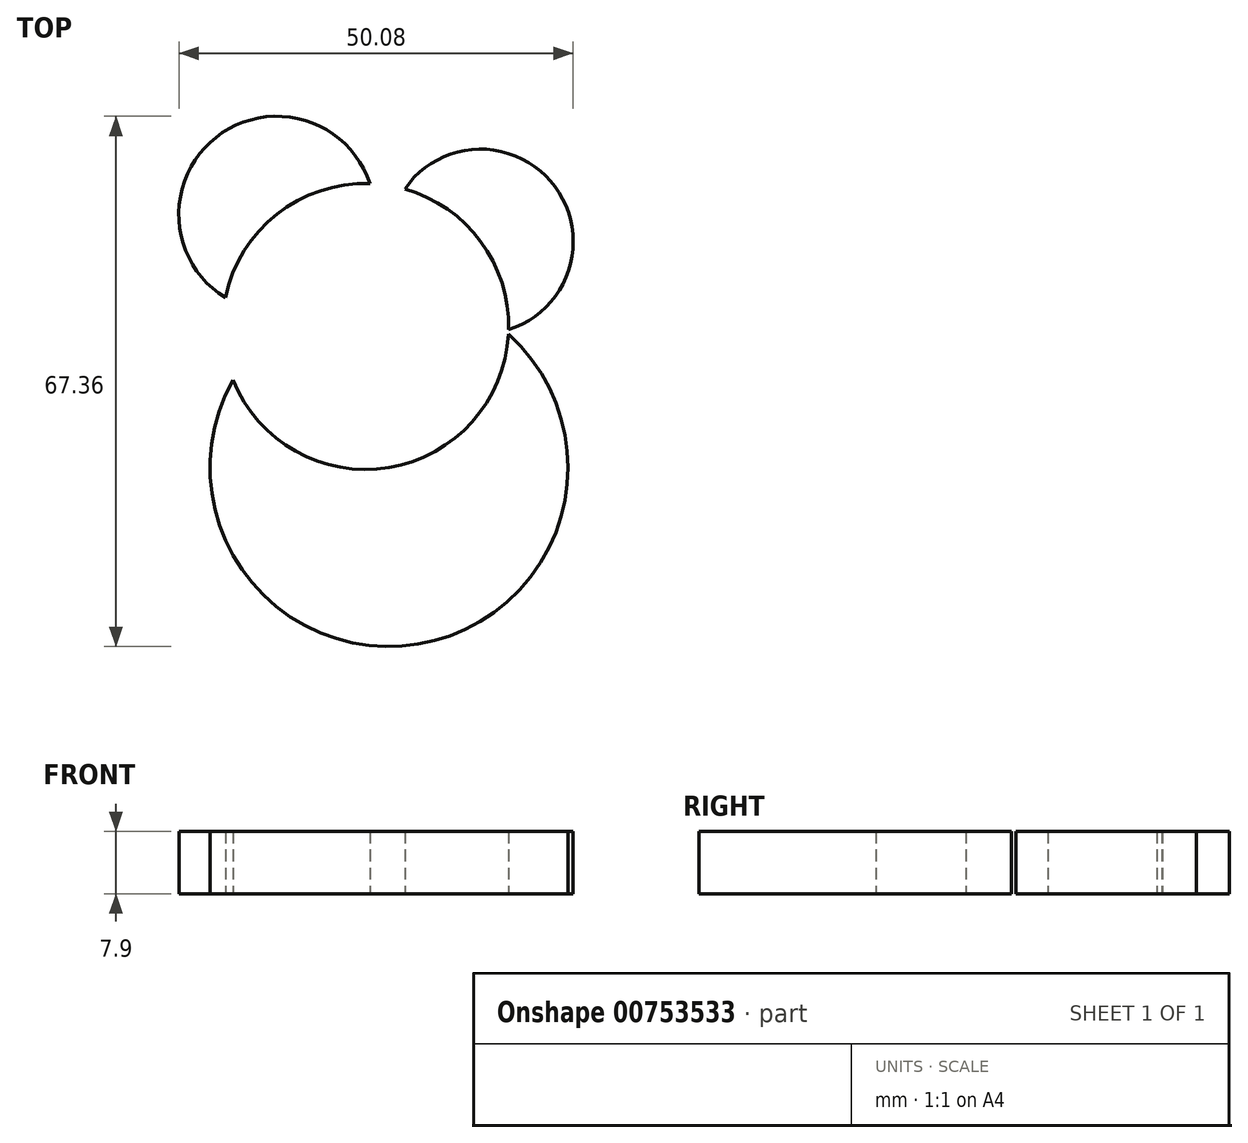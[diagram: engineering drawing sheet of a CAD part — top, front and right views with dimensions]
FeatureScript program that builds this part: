
annotation { "Feature Type Name" : "Feature", "Feature Type Description" : "" }
export const myFeature = defineFeature(function(context is Context, id is Id, definition is map)
    precondition{}
    {
        {
            var Q0;
            Q0=qCreatedBy(makeId("Top.planeOp"),FACE);
            var sketch = newSketch(context, id + "F0", { "sketchPlane" : qUnion([Q0])});
            skCircle(sketch, "E0", {"center": v(0, 0) * mm, "radius": 18.17 * mm});
            skCircle(sketch, "E1", {"center": v(-11.27, 14.25) * mm, "radius": 12.45 * mm});
            skCircle(sketch, "E2", {"center": v(14.62, 10.78) * mm, "radius": 11.74 * mm});
            skCircle(sketch, "E3", {"center": v(2.97, -17.92) * mm, "radius": 22.73 * mm});
            skSolve(sketch);
        }
        {
            var Q0;
            {var subQ0=sQuery(id+"F0.wireOp",EDGE,"E1");var subQ1=sQuery(id+"F0.wireOp",EDGE,"E0");var subQ2=makeQuery(id+"F0.imprint","INTERSECT",VERTEX,{"disambiguationData":[OD(0.0)],"derivedFrom":[subQ1,subQ0]});Q0=makeQuery(id+"F0.imprint","IMPRINT",FACE,{"disambiguationData":[TD([[makeQuery(id+"F0.imprint","IMPRINT",EDGE,{"disambiguationData":[TD([[subQ2,-1.0]])],"derivedFrom":subQ1}),-1.0]])]});}
            var Q1;
            {var subQ0=sQuery(id+"F0.wireOp",EDGE,"E3");var subQ1=sQuery(id+"F0.wireOp",EDGE,"E0");var subQ2=makeQuery(id+"F0.imprint","INTERSECT",VERTEX,{"disambiguationData":[OD(0.0)],"derivedFrom":[subQ1,subQ0]});Q1=makeQuery(id+"F0.imprint","IMPRINT",FACE,{"disambiguationData":[TD([[makeQuery(id+"F0.imprint","IMPRINT",EDGE,{"disambiguationData":[TD([[subQ2,-1.0]])],"derivedFrom":subQ1}),-1.0]])]});}
            var Q2;
            {var subQ0=sQuery(id+"F0.wireOp",EDGE,"E2");var subQ1=sQuery(id+"F0.wireOp",EDGE,"E0");var subQ2=makeQuery(id+"F0.imprint","INTERSECT",VERTEX,{"disambiguationData":[OD(0.0)],"derivedFrom":[subQ1,subQ0]});Q2=makeQuery(id+"F0.imprint","IMPRINT",FACE,{"disambiguationData":[TD([[makeQuery(id+"F0.imprint","IMPRINT",EDGE,{"disambiguationData":[TD([[subQ2,1.0]])],"derivedFrom":subQ1}),-1.0]])]});}
            extrude(context, id + "F1", {"entities" : qUnion([Q0, Q1, Q2]), "depth" : 7.9 * mm, "offsetDistance" : 25 * mm});
        }
    });
